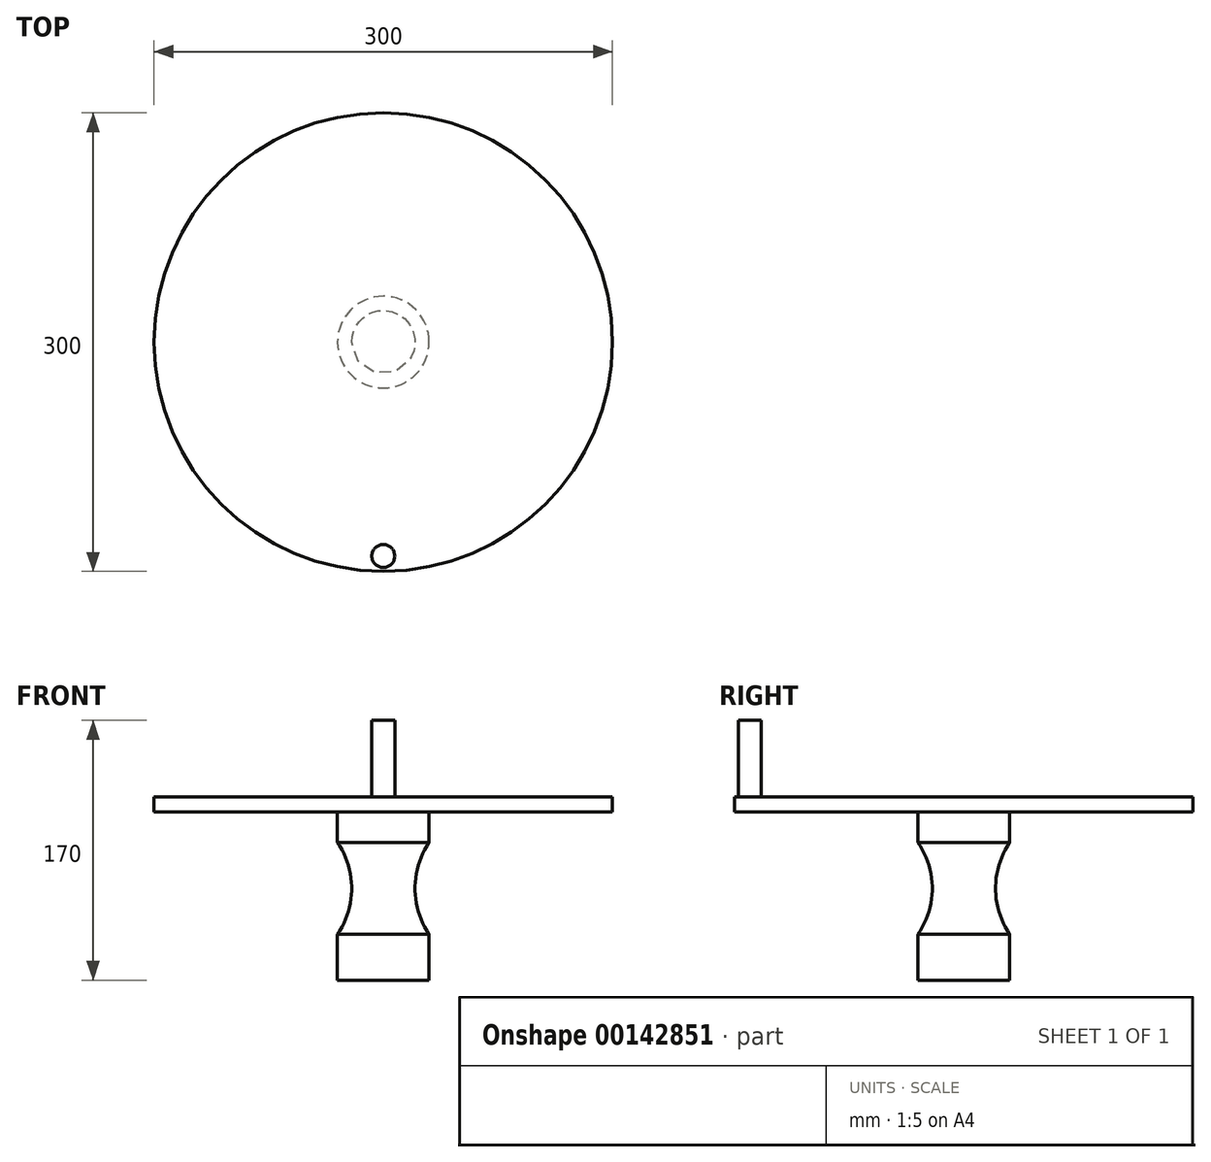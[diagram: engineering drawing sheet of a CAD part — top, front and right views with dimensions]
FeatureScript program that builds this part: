
annotation { "Feature Type Name" : "Feature", "Feature Type Description" : "" }
export const myFeature = defineFeature(function(context is Context, id is Id, definition is map)
    precondition{}
    {
        {
            var Q0;
            Q0=qCreatedBy(makeId("Front.planeOp"),FACE);
            var sketch = newSketch(context, id + "F0", { "sketchPlane" : qUnion([Q0])});
            skLineSegment(sketch, "E0", {"start": v(-30, 0) * mm, "end": v(-150, 0) * mm});
            skLineSegment(sketch, "E1", {"start": v(-150, 0) * mm, "end": v(-150, 10) * mm});
            skLineSegment(sketch, "E2", {"start": v(-150, 10) * mm, "end": v(0, 10) * mm});
            skLineSegment(sketch, "E3", {"start": v(0, 10) * mm, "end": v(0, 0) * mm});
            skLineSegment(sketch, "E4", {"start": v(-30, 0) * mm, "end": v(-30, -20) * mm});
            skLineSegment(sketch, "E5", {"start": v(-30, -110) * mm, "end": v(0, -110) * mm});
            skLineSegment(sketch, "E6", {"start": v(0, -110) * mm, "end": v(0, 0) * mm});
            skLineSegment(sketch, "E7.trimOffspring", {"start": v(-30, -80) * mm, "end": v(-30, -110) * mm});
            skArc(sketch, "E8", {"start": v(-30, -80) * mm, "mid": v(-20.7, -50) * mm, "end": v(-30, -20) * mm});
            skSolve(sketch);
        }
        {
            var Q0;
            Q0 = qSketchRegion(id + "F0", true);
            var Q1;
            Q1=sQuery(id+"F0.wireOp",EDGE,"E6");
            revolve(context, id + "F1", {"entities" : qUnion([Q0]), "axis" : qUnion([Q1]), "revolveType" : RevolveType.FULL});
        }
        {
            var Q0;
            Q0=makeQuery(id+"F1.opRevolve","SWEPT_FACE",FACE,{"disambiguationData":[OSD([sQuery(id+"F0.wireOp",EDGE,"E2")])]});
            var sketch = newSketch(context, id + "F2", { "sketchPlane" : qUnion([Q0])});
            skCircle(sketch, "E9", {"center": v(0, -140) * mm, "radius": 7.5 * mm});
            skSolve(sketch);
        }
        {
            var Q0;
            Q0 = qSketchRegion(id + "F2", true);
            extrude(context, id + "F3", {"entities" : qUnion([Q0]), "operationType" : NewBodyOperationType.ADD, "depth" : 50 * mm});
        }
    });
